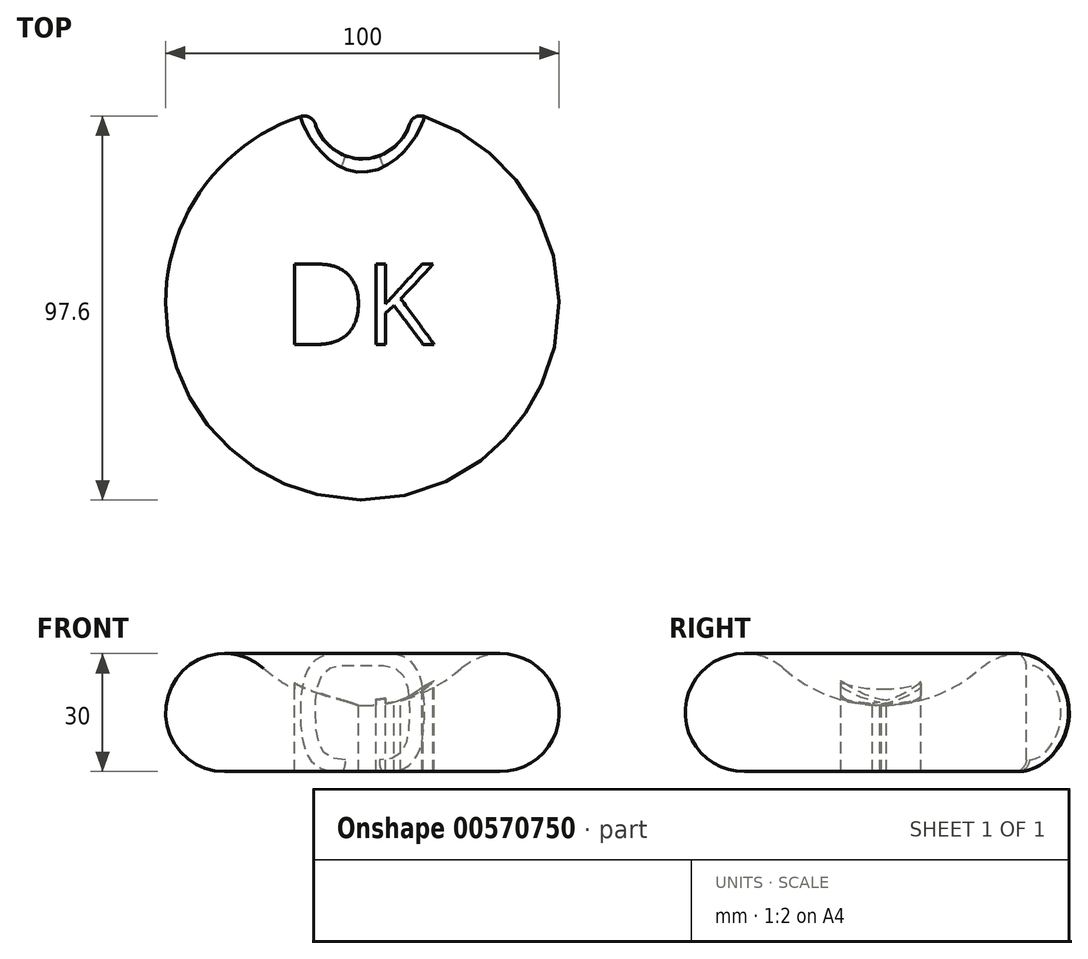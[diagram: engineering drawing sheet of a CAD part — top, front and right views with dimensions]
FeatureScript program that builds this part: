
annotation { "Feature Type Name" : "Feature", "Feature Type Description" : "" }
export const myFeature = defineFeature(function(context is Context, id is Id, definition is map)
    precondition{}
    {
        {
            var Q0;
            Q0=qCreatedBy(makeId("Front.planeOp"),FACE);
            var sketch = newSketch(context, id + "F0", { "sketchPlane" : qUnion([Q0])});
            skArc(sketch, "E0", {"start": v(-25.09, 11.26) * mm, "mid": v(-13.4, 4.23) * mm, "end": v(0, 1.79) * mm});
            skArc(sketch, "E1", {"start": v(-25.09, 11.26) * mm, "mid": v(-49.03, 5.3) * mm, "end": v(-35, -15) * mm});
            skLineSegment(sketch, "E2", {"start": v(-35, -15) * mm, "end": v(0, -15) * mm});
            skLineSegment(sketch, "E3", {"start": v(0, -15) * mm, "end": v(0, 1.79) * mm});
            skSolve(sketch);
        }
        {
            var Q0;
            Q0=makeQuery(id+"F0.imprint","IMPRINT",FACE,{"disambiguationData":[TD([[makeQuery(id+"F0.imprint","IMPRINT",EDGE,{"derivedFrom":sQuery(id+"F0.wireOp",EDGE,"E0")}),-1.0]])]});
            var Q1;
            Q1=sQuery(id+"F0.wireOp",EDGE,"E3");
            revolve(context, id + "F1", {"entities" : qUnion([Q0]), "axis" : qUnion([Q1]), "revolveType" : RevolveType.FULL});
        }
        {
            var Q0;
            Q0=qCreatedBy(makeId("Top.planeOp"),FACE);
            cPlane(context, id + "F2", {"entities" : qUnion([Q0]), "cplaneType" : CPlaneType.OFFSET, "offset" : 15 * mm, "width" : 150 * mm, "height" : 150 * mm});
        }
        {
            var Q0;
            Q0=qCreatedBy(id+"F2.planeOp",FACE);
            var sketch = newSketch(context, id + "F3", { "sketchPlane" : qUnion([Q0])});
            skText(sketch, "E4", { "text": "DK", "fontName": "OpenSans-Regular.ttf"});
            const initialGuessF3  = {"E4": [-0.02009, -0.01046, 1, 0, 0.02055]};
            skSetInitialGuess(sketch, initialGuessF3);
            skSolve(sketch);
        }
        {
            var Q0;
            Q0 = qSketchRegion(id + "F3", true);
            var Q1;
            Q1=makeQuery(id+"F1.opRevolve","SWEPT_FACE",FACE,{"disambiguationData":[OSD([sQuery(id+"F0.wireOp",EDGE,"E2")])]});
            extrude(context, id + "F4", {"entities" : qUnion([Q0]), "operationType" : NewBodyOperationType.REMOVE, "endBound" : BoundingType.UP_TO_SURFACE, "oppositeDirection" : true, "depth" : 25 * mm, "endBoundEntityFace" : qUnion([Q1]), "offsetDistance" : 25 * mm});
        }
        {
            var Q0;
            Q0=makeQuery(id+"F3.imprint","IMPRINT",FACE,{"disambiguationData":[TD([[makeQuery(id+"F3.imprint","IMPRINT",EDGE,{"derivedFrom":sQuery(id+"F3.wireOp",EDGE,"E4.sketch_text.stroke-7")}),1.0]])]});
            var Q1;
            Q1=makeQuery(id+"F4.boolean.opBoolean","SPLIT",FACE,{"disambiguationData":[TD([makeQuery(id+"F1.opRevolve","SWEPT_FACE",FACE,{"disambiguationData":[OSD([sQuery(id+"F0.wireOp",EDGE,"E1")])]})])],"derivedFrom":makeQuery(id+"F1.opRevolve","SWEPT_FACE",FACE,{"disambiguationData":[OSD([sQuery(id+"F0.wireOp",EDGE,"E2")])]})});
            extrude(context, id + "F5", {"entities" : qUnion([Q0]), "operationType" : NewBodyOperationType.REMOVE, "endBound" : BoundingType.UP_TO_SURFACE, "oppositeDirection" : true, "depth" : 25 * mm, "endBoundEntityFace" : qUnion([Q1]), "offsetDistance" : 25 * mm});
        }
        {
            var Q0;
            Q0=qCreatedBy(id+"F2.planeOp",FACE);
            var sketch = newSketch(context, id + "F6", { "sketchPlane" : qUnion([Q0])});
            skCircle(sketch, "E5", {"center": v(0, 49.15) * mm, "radius": 12.5 * mm});
            skSolve(sketch);
        }
        {
            var Q0;
            Q0=makeQuery(id+"F6.imprint","IMPRINT",FACE,{"disambiguationData":[TD([[makeQuery(id+"F6.imprint","IMPRINT",EDGE,{"derivedFrom":sQuery(id+"F6.wireOp",EDGE,"E5")}),1.0]])]});
            var Q1;
            Q1=makeQuery(id+"F1.opRevolve","SWEPT_FACE",FACE,{"disambiguationData":[OSD([sQuery(id+"F0.wireOp",EDGE,"E1")])]});
            extrude(context, id + "F7", {"entities" : qUnion([Q0]), "operationType" : NewBodyOperationType.REMOVE, "oppositeDirection" : true, "depth" : 40.1 * mm, "endBoundEntityFace" : qUnion([Q1]), "offsetDistance" : 25 * mm});
        }
        {
            var Q0;
            Q0=makeQuery(id+"F7.boolean.opBoolean","INTERSECT",EDGE,{"derivedFrom":[makeQuery(id+"F1.opRevolve","SWEPT_FACE",FACE,{"disambiguationData":[OSD([sQuery(id+"F0.wireOp",EDGE,"E1")])]}),makeQuery(id+"F7.opExtrude","SWEPT_FACE",FACE,{"disambiguationData":[OSD([sQuery(id+"F6.wireOp",EDGE,"E5")])]})]});
            fillet(context, id + "F8", {"entities" : qUnion([Q0]), "radius" : 3 * mm, "tangentPropagation" : true, "allowEdgeOverflow" : false});
        }
    });
